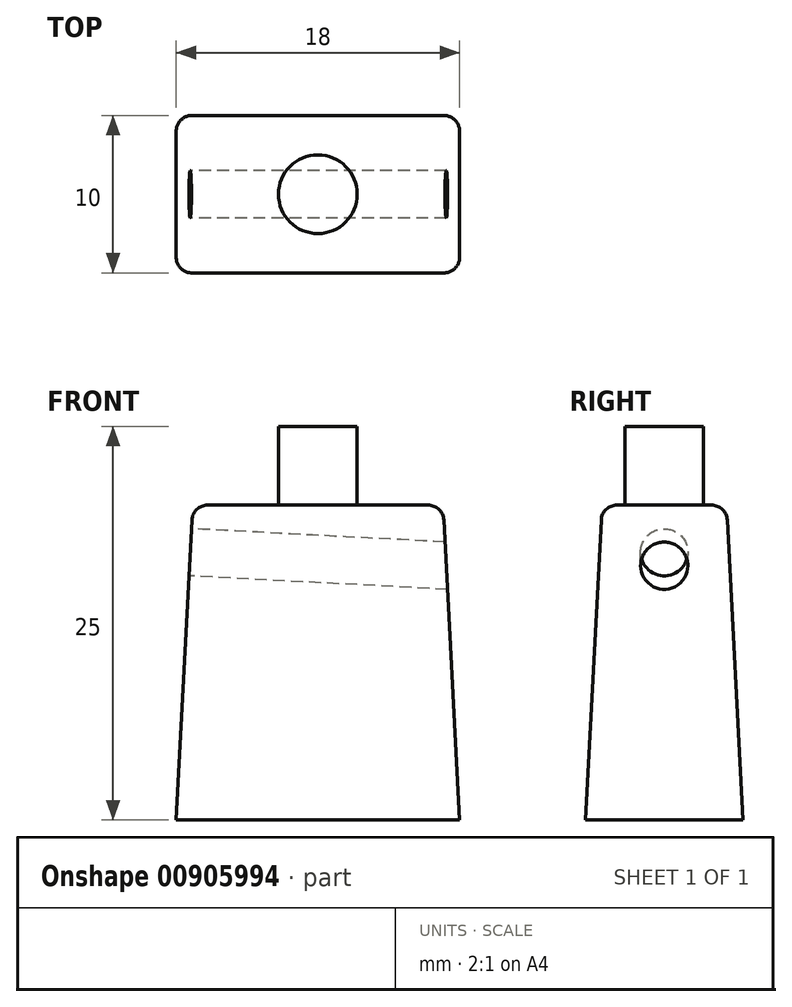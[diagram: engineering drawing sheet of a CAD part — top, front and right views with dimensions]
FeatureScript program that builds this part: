
annotation { "Feature Type Name" : "Feature", "Feature Type Description" : "" }
export const myFeature = defineFeature(function(context is Context, id is Id, definition is map)
    precondition{}
    {
        {
            var Q0;
            Q0=qCreatedBy(makeId("Top.planeOp"),FACE);
            var sketch = newSketch(context, id + "F0", { "sketchPlane" : qUnion([Q0])});
            skLineSegment(sketch, "E0.bottom", {"start": v(9, -5) * mm, "end": v(-9, -5) * mm});
            skLineSegment(sketch, "E0.top", {"start": v(9, 5) * mm, "end": v(-9, 5) * mm});
            skLineSegment(sketch, "E0.left", {"start": v(9, -5) * mm, "end": v(9, 5) * mm});
            skLineSegment(sketch, "E0.right", {"start": v(-9, -5) * mm, "end": v(-9, 5) * mm});
            skPoint(sketch, "E0.middle", {"position": v(0, 0) * mm});
            skSolve(sketch);
        }
        {
            var Q0;
            Q0=makeQuery(id+"F0.imprint","IMPRINT",FACE,{"disambiguationData":[TD([[makeQuery(id+"F0.imprint","IMPRINT",EDGE,{"derivedFrom":sQuery(id+"F0.wireOp",EDGE,"E0.bottom")}),-1.0]])]});
            extrude(context, id + "F1", {"entities" : qUnion([Q0]), "depth" : 20 * mm, "offsetDistance" : 25.4 * mm, "hasDraft" : true, "draftAngle" : 3 * degree, "draftPullDirection" : true});
        }
        {
            var Q0;
            Q0=makeQuery(id+"F1.opExtrude","CAP_FACE",FACE,{"disambiguationData":[OSD([sQuery(id+"F0.wireOp",EDGE,"E0.bottom"),sQuery(id+"F0.wireOp",EDGE,"E0.top"),sQuery(id+"F0.wireOp",EDGE,"E0.left"),sQuery(id+"F0.wireOp",EDGE,"E0.right")])],"isStart":false});
            var sketch = newSketch(context, id + "F2", { "sketchPlane" : qUnion([Q0])});
            skCircle(sketch, "E1", {"center": v(0, 0) * mm, "radius": 2.5 * mm});
            skSolve(sketch);
        }
        {
            var Q0;
            Q0=makeQuery(id+"F2.imprint","IMPRINT",FACE,{"disambiguationData":[TD([[makeQuery(id+"F2.imprint","IMPRINT",EDGE,{"derivedFrom":sQuery(id+"F2.wireOp",EDGE,"E1")}),1.0]])]});
            extrude(context, id + "F3", {"entities" : qUnion([Q0]), "operationType" : NewBodyOperationType.ADD, "depth" : 5 * mm, "offsetDistance" : 25.4 * mm});
        }
        {
            var Q0;
            Q0=makeQuery(id+"F1.opExtrude","SWEPT_FACE",FACE,{"disambiguationData":[OSD([sQuery(id+"F0.wireOp",EDGE,"E0.right")])]});
            var sketch = newSketch(context, id + "F4", { "sketchPlane" : qUnion([Q0])});
            skCircle(sketch, "E2", {"center": v(0, 16.56) * mm, "radius": 1.5 * mm});
            skSolve(sketch);
        }
        {
            var Q0;
            Q0=makeQuery(id+"F1.opExtrude","SWEPT_EDGE",EDGE,{"disambiguationData":[OSD([sQuery(id+"F0.wireOp",EDGE,"E0.top"),sQuery(id+"F0.wireOp",EDGE,"E0.left")])]});
            var Q1;
            Q1=makeQuery(id+"F1.opExtrude","CAP_EDGE",EDGE,{"disambiguationData":[OSD([sQuery(id+"F0.wireOp",EDGE,"E0.top")])],"isStart":false});
            var Q2;
            Q2=makeQuery(id+"F1.opExtrude","SWEPT_EDGE",EDGE,{"disambiguationData":[OSD([sQuery(id+"F0.wireOp",EDGE,"E0.top"),sQuery(id+"F0.wireOp",EDGE,"E0.right")])]});
            var Q3;
            Q3=makeQuery(id+"F1.opExtrude","CAP_EDGE",EDGE,{"disambiguationData":[OSD([sQuery(id+"F0.wireOp",EDGE,"E0.right")])],"isStart":false});
            var Q4;
            Q4=makeQuery(id+"F1.opExtrude","SWEPT_EDGE",EDGE,{"disambiguationData":[OSD([sQuery(id+"F0.wireOp",EDGE,"E0.bottom"),sQuery(id+"F0.wireOp",EDGE,"E0.right")])]});
            var Q5;
            Q5=makeQuery(id+"F1.opExtrude","SWEPT_EDGE",EDGE,{"disambiguationData":[OSD([sQuery(id+"F0.wireOp",EDGE,"E0.bottom"),sQuery(id+"F0.wireOp",EDGE,"E0.left")])]});
            var Q6;
            Q6=makeQuery(id+"F1.opExtrude","CAP_EDGE",EDGE,{"disambiguationData":[OSD([sQuery(id+"F0.wireOp",EDGE,"E0.bottom")])],"isStart":false});
            var Q7;
            Q7=makeQuery(id+"F1.opExtrude","CAP_EDGE",EDGE,{"disambiguationData":[OSD([sQuery(id+"F0.wireOp",EDGE,"E0.left")])],"isStart":false});
            fillet(context, id + "F5", {"entities" : qUnion([Q0, Q1, Q2, Q3, Q4, Q5, Q6, Q7]), "radius" : 1 * mm, "tangentPropagation" : true, "allowEdgeOverflow" : false});
        }
        {
            var Q0;
            Q0=makeQuery(id+"F4.imprint","IMPRINT",FACE,{"disambiguationData":[TD([[makeQuery(id+"F4.imprint","IMPRINT",EDGE,{"derivedFrom":sQuery(id+"F4.wireOp",EDGE,"E2")}),1.0]])]});
            extrude(context, id + "F6", {"entities" : qUnion([Q0]), "operationType" : NewBodyOperationType.REMOVE, "oppositeDirection" : true, "depth" : 25.4 * mm, "offsetDistance" : 25.4 * mm});
        }
    });
